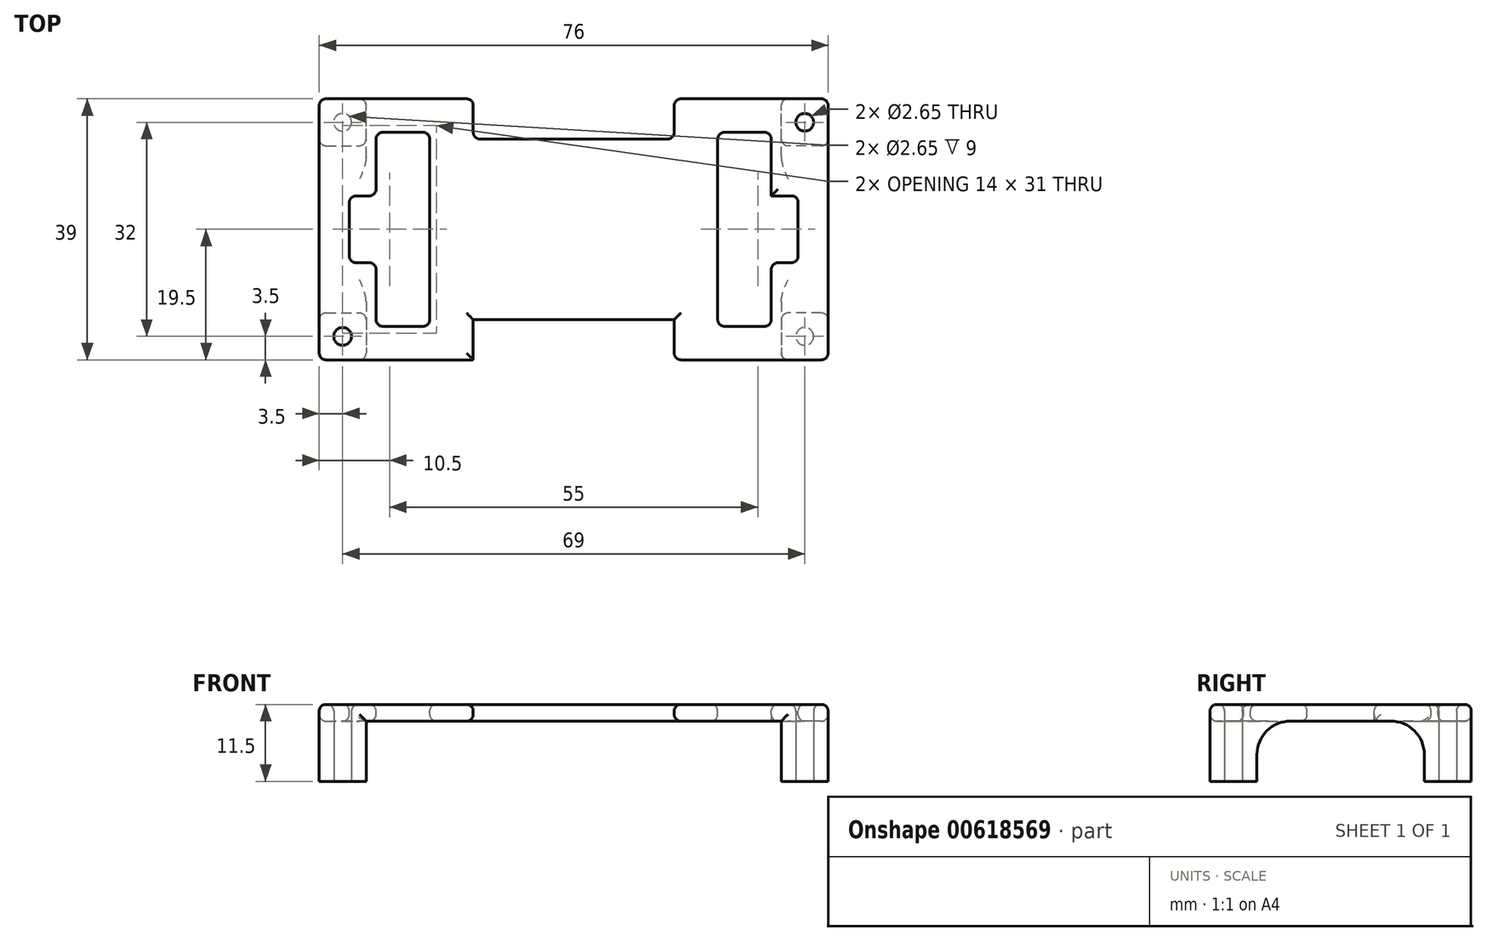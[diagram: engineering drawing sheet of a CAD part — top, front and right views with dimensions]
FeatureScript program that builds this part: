
annotation { "Feature Type Name" : "Feature", "Feature Type Description" : "" }
export const myFeature = defineFeature(function(context is Context, id is Id, definition is map)
    precondition{}
    {
        {
            var Q0;
            Q0=qCreatedBy(makeId("Top.planeOp"),FACE);
            var sketch = newSketch(context, id + "F0", { "sketchPlane" : qUnion([Q0])});
            skCircle(sketch, "E0", {"center": v(-34.5, 16) * mm, "radius": 1.5 * mm});
            skCircle(sketch, "E1", {"center": v(-34.5, 16) * mm, "radius": 1.32 * mm});
            skLineSegment(sketch, "E2", {"start": v(-38, 0) * mm, "end": v(-38, 19.5) * mm});
            skLineSegment(sketch, "E3", {"start": v(-38, 19.5) * mm, "end": v(0, 19.5) * mm});
            skLineSegment(sketch, "E4.MirrorCS", {"start": v(38, 19.5) * mm, "end": v(0, 19.5) * mm});
            skLineSegment(sketch, "E5.MirrorCS", {"start": v(-38, -19.5) * mm, "end": v(0, -19.5) * mm});
            skLineSegment(sketch, "E6.MirrorCS", {"start": v(38, -19.5) * mm, "end": v(0, -19.5) * mm});
            skLineSegment(sketch, "E7.MirrorCS", {"start": v(38, 0) * mm, "end": v(38, 19.5) * mm});
            skLineSegment(sketch, "E8.MirrorCS", {"start": v(-38, 0) * mm, "end": v(-38, -19.5) * mm});
            skLineSegment(sketch, "E9.MirrorCS", {"start": v(38, 0) * mm, "end": v(38, -19.5) * mm});
            skLineSegment(sketch, "E10", {"start": v(-38, 12.5) * mm, "end": v(-31, 12.5) * mm});
            skLineSegment(sketch, "E11", {"start": v(-31, 12.5) * mm, "end": v(-31, 19.5) * mm});
            skLineSegment(sketch, "E12.MirrorCS", {"start": v(31, 12.5) * mm, "end": v(31, 19.5) * mm});
            skLineSegment(sketch, "E13.MirrorCS", {"start": v(38, 12.5) * mm, "end": v(31, 12.5) * mm});
            skLineSegment(sketch, "E14.MirrorCS", {"start": v(38, -12.5) * mm, "end": v(31, -12.5) * mm});
            skLineSegment(sketch, "E15.MirrorCS", {"start": v(31, -12.5) * mm, "end": v(31, -19.5) * mm});
            skLineSegment(sketch, "E16.MirrorCS", {"start": v(-38, -12.5) * mm, "end": v(-31, -12.5) * mm});
            skLineSegment(sketch, "E17.MirrorCS", {"start": v(-31, -12.5) * mm, "end": v(-31, -19.5) * mm});
            skCircle(sketch, "E18.MirrorC", {"center": v(34.5, 16) * mm, "radius": 1.32 * mm});
            skCircle(sketch, "E19.MirrorC", {"center": v(-34.5, -16) * mm, "radius": 1.32 * mm});
            skCircle(sketch, "E20.MirrorC", {"center": v(34.5, -16) * mm, "radius": 1.32 * mm});
            skSolve(sketch);
        }
        {
            var Q0;
            Q0=makeQuery(id+"F0.imprint","IMPRINT",FACE,{"disambiguationData":[TD([[makeQuery(id+"F0.imprint","IMPRINT",EDGE,{"derivedFrom":sQuery(id+"F0.wireOp",EDGE,"E0")}),-1.0]])]});
            var Q1;
            Q1=makeQuery(id+"F0.imprint","IMPRINT",FACE,{"disambiguationData":[TD([[makeQuery(id+"F0.imprint","IMPRINT",EDGE,{"derivedFrom":sQuery(id+"F0.wireOp",EDGE,"9949ebb8-f0cd-4d5a-9bb0-dda6fca556a90.MirrorC")}),1.0]])]});
            var Q2;
            Q2=makeQuery(id+"F0.imprint","IMPRINT",FACE,{"disambiguationData":[TD([[makeQuery(id+"F0.imprint","IMPRINT",EDGE,{"derivedFrom":sQuery(id+"F0.wireOp",EDGE,"ff901f8d-6ad3-493e-a052-18a1848739b60.MirrorC")}),1.0]])]});
            var Q3;
            Q3=makeQuery(id+"F0.imprint","IMPRINT",FACE,{"disambiguationData":[TD([[makeQuery(id+"F0.imprint","IMPRINT",EDGE,{"derivedFrom":sQuery(id+"F0.wireOp",EDGE,"884a96e5-8a82-4bf0-9c84-4d8750a24e620.MirrorC")}),-1.0]])]});
            var Q4;
            {var subQ0=sQuery(id+"F0.wireOp",EDGE,"E16.MirrorCS");Q4=makeQuery(id+"F0.imprint","IMPRINT",FACE,{"disambiguationData":[TD([[makeQuery(id+"F0.imprint","IMPRINT",EDGE,{"derivedFrom":subQ0}),-1.0]])]});}
            var Q5;
            {var subQ1=sQuery(id+"F0.wireOp",EDGE,"E14.MirrorCS");Q5=makeQuery(id+"F0.imprint","IMPRINT",FACE,{"disambiguationData":[TD([[makeQuery(id+"F0.imprint","IMPRINT",EDGE,{"derivedFrom":subQ1}),1.0]])]});}
            var Q6;
            {var subQ0=sQuery(id+"F0.wireOp",EDGE,"E12.MirrorCS");Q6=makeQuery(id+"F0.imprint","IMPRINT",FACE,{"disambiguationData":[TD([[makeQuery(id+"F0.imprint","IMPRINT",EDGE,{"derivedFrom":subQ0}),-1.0]])]});}
            var Q7;
            Q7=makeQuery(id+"F0.imprint","IMPRINT",FACE,{"disambiguationData":[TD([[makeQuery(id+"F0.imprint","IMPRINT",EDGE,{"derivedFrom":sQuery(id+"F0.wireOp",EDGE,"E0")}),1.0]])]});
            extrude(context, id + "F1", {"entities" : qUnion([Q0, Q1, Q2, Q3, Q4, Q5, Q6, Q7]), "depth" : 9 * mm, "offsetDistance" : 25 * mm});
        }
        {
            var Q0;
            {var subQ13=sQuery(id+"F0.wireOp",EDGE,"E10");Q0=makeQuery(id+"F0.imprint","IMPRINT",FACE,{"disambiguationData":[TD([[makeQuery(id+"F0.imprint","IMPRINT",EDGE,{"derivedFrom":subQ13}),-1.0]])]});}
            var Q1;
            Q1=makeQuery(id+"F0.imprint","IMPRINT",FACE,{"disambiguationData":[TD([[makeQuery(id+"F0.imprint","IMPRINT",EDGE,{"derivedFrom":sQuery(id+"F0.wireOp",EDGE,"ff901f8d-6ad3-493e-a052-18a1848739b60.MirrorC")}),1.0]])]});
            var Q2;
            Q2=makeQuery(id+"F0.imprint","IMPRINT",FACE,{"disambiguationData":[TD([[makeQuery(id+"F0.imprint","IMPRINT",EDGE,{"derivedFrom":sQuery(id+"F0.wireOp",EDGE,"884a96e5-8a82-4bf0-9c84-4d8750a24e620.MirrorC")}),-1.0]])]});
            var Q3;
            Q3=makeQuery(id+"F0.imprint","IMPRINT",FACE,{"disambiguationData":[TD([[makeQuery(id+"F0.imprint","IMPRINT",EDGE,{"derivedFrom":sQuery(id+"F0.wireOp",EDGE,"ff901f8d-6ad3-493e-a052-18a1848739b60.MirrorC")}),-1.0]])]});
            var Q4;
            Q4=makeQuery(id+"F0.imprint","IMPRINT",FACE,{"disambiguationData":[TD([[makeQuery(id+"F0.imprint","IMPRINT",EDGE,{"derivedFrom":sQuery(id+"F0.wireOp",EDGE,"884a96e5-8a82-4bf0-9c84-4d8750a24e620.MirrorC")}),1.0]])]});
            var Q5;
            Q5=makeQuery(id+"F0.imprint","IMPRINT",FACE,{"disambiguationData":[TD([[makeQuery(id+"F0.imprint","IMPRINT",EDGE,{"derivedFrom":sQuery(id+"F0.wireOp",EDGE,"9949ebb8-f0cd-4d5a-9bb0-dda6fca556a90.MirrorC")}),1.0]])]});
            var Q6;
            Q6=makeQuery(id+"F0.imprint","IMPRINT",FACE,{"disambiguationData":[TD([[makeQuery(id+"F0.imprint","IMPRINT",EDGE,{"derivedFrom":sQuery(id+"F0.wireOp",EDGE,"9949ebb8-f0cd-4d5a-9bb0-dda6fca556a90.MirrorC")}),-1.0]])]});
            var Q7;
            {var subQ0=sQuery(id+"F0.wireOp",EDGE,"E12.MirrorCS");Q7=makeQuery(id+"F0.imprint","IMPRINT",FACE,{"disambiguationData":[TD([[makeQuery(id+"F0.imprint","IMPRINT",EDGE,{"derivedFrom":subQ0}),-1.0]])]});}
            var Q8;
            {var subQ1=sQuery(id+"F0.wireOp",EDGE,"E14.MirrorCS");Q8=makeQuery(id+"F0.imprint","IMPRINT",FACE,{"disambiguationData":[TD([[makeQuery(id+"F0.imprint","IMPRINT",EDGE,{"derivedFrom":subQ1}),1.0]])]});}
            var Q9;
            Q9=makeQuery(id+"F0.imprint","IMPRINT",FACE,{"disambiguationData":[TD([[makeQuery(id+"F0.imprint","IMPRINT",EDGE,{"derivedFrom":sQuery(id+"F0.wireOp",EDGE,"E0")}),-1.0]])]});
            var Q10;
            Q10=makeQuery(id+"F0.imprint","IMPRINT",FACE,{"disambiguationData":[TD([[makeQuery(id+"F0.imprint","IMPRINT",EDGE,{"derivedFrom":sQuery(id+"F0.wireOp",EDGE,"E0")}),1.0]])]});
            var Q11;
            Q11=makeQuery(id+"F0.imprint","IMPRINT",FACE,{"disambiguationData":[TD([[makeQuery(id+"F0.imprint","IMPRINT",EDGE,{"derivedFrom":sQuery(id+"F0.wireOp",EDGE,"E1")}),1.0]])]});
            var Q12;
            Q12=makeQuery(id+"F0.imprint","IMPRINT",FACE,{"disambiguationData":[TD([[makeQuery(id+"F0.imprint","IMPRINT",EDGE,{"derivedFrom":sQuery(id+"F0.wireOp",EDGE,"E18.MirrorC")}),-1.0]])]});
            var Q13;
            Q13=makeQuery(id+"F0.imprint","IMPRINT",FACE,{"disambiguationData":[TD([[makeQuery(id+"F0.imprint","IMPRINT",EDGE,{"derivedFrom":sQuery(id+"F0.wireOp",EDGE,"E20.MirrorC")}),1.0]])]});
            var Q14;
            {var subQ0=sQuery(id+"F0.wireOp",EDGE,"E16.MirrorCS");Q14=makeQuery(id+"F0.imprint","IMPRINT",FACE,{"disambiguationData":[TD([[makeQuery(id+"F0.imprint","IMPRINT",EDGE,{"derivedFrom":subQ0}),-1.0]])]});}
            var Q15;
            Q15=makeQuery(id+"F0.imprint","IMPRINT",FACE,{"disambiguationData":[TD([[makeQuery(id+"F0.imprint","IMPRINT",EDGE,{"derivedFrom":sQuery(id+"F0.wireOp",EDGE,"E19.MirrorC")}),-1.0]])]});
            extrude(context, id + "F2", {"entities" : qUnion([Q0, Q1, Q2, Q3, Q4, Q5, Q6, Q7, Q8, Q9, Q10, Q11, Q12, Q13, Q14, Q15]), "depth" : 11.5 * mm, "offsetDistance" : 25 * mm, "hasSecondDirection" : true, "secondDirectionOppositeDirection" : true, "secondDirectionDepth" : -9 * mm});
        }
        {
            var Q0;
            Q0=makeQuery(id+"F1.opExtrude","SWEPT_BODY",BODY,{"disambiguationData":[OSD([sQuery(id+"F0.wireOp",EDGE,"ff901f8d-6ad3-493e-a052-18a1848739b60.MirrorC"),sQuery(id+"F0.wireOp",EDGE,"E5.MirrorCS"),sQuery(id+"F0.wireOp",EDGE,"E8.MirrorCS"),sQuery(id+"F0.wireOp",EDGE,"E16.MirrorCS"),sQuery(id+"F0.wireOp",EDGE,"E17.MirrorCS")])]});
            var Q1;
            Q1=makeQuery(id+"F2.opExtrude","SWEPT_BODY",BODY,{"disambiguationData":[OSD([sQuery(id+"F0.wireOp",EDGE,"E2"),sQuery(id+"F0.wireOp",EDGE,"E3"),sQuery(id+"F0.wireOp",EDGE,"E4.MirrorCS"),sQuery(id+"F0.wireOp",EDGE,"E5.MirrorCS"),sQuery(id+"F0.wireOp",EDGE,"E6.MirrorCS"),sQuery(id+"F0.wireOp",EDGE,"E7.MirrorCS"),sQuery(id+"F0.wireOp",EDGE,"E8.MirrorCS"),sQuery(id+"F0.wireOp",EDGE,"E9.MirrorCS")])]});
            var Q2;
            Q2=makeQuery(id+"F1.opExtrude","SWEPT_BODY",BODY,{"disambiguationData":[OSD([sQuery(id+"F0.wireOp",EDGE,"E0"),sQuery(id+"F0.wireOp",EDGE,"E2"),sQuery(id+"F0.wireOp",EDGE,"E3"),sQuery(id+"F0.wireOp",EDGE,"E10"),sQuery(id+"F0.wireOp",EDGE,"E11")])]});
            var Q3;
            Q3=makeQuery(id+"F1.opExtrude","SWEPT_BODY",BODY,{"disambiguationData":[OSD([sQuery(id+"F0.wireOp",EDGE,"884a96e5-8a82-4bf0-9c84-4d8750a24e620.MirrorC"),sQuery(id+"F0.wireOp",EDGE,"E6.MirrorCS"),sQuery(id+"F0.wireOp",EDGE,"E9.MirrorCS"),sQuery(id+"F0.wireOp",EDGE,"E14.MirrorCS"),sQuery(id+"F0.wireOp",EDGE,"E15.MirrorCS")])]});
            var Q4;
            Q4=makeQuery(id+"F1.opExtrude","SWEPT_BODY",BODY,{"disambiguationData":[OSD([sQuery(id+"F0.wireOp",EDGE,"9949ebb8-f0cd-4d5a-9bb0-dda6fca556a90.MirrorC"),sQuery(id+"F0.wireOp",EDGE,"E4.MirrorCS"),sQuery(id+"F0.wireOp",EDGE,"E7.MirrorCS"),sQuery(id+"F0.wireOp",EDGE,"E12.MirrorCS"),sQuery(id+"F0.wireOp",EDGE,"E13.MirrorCS")])]});
            booleanBodies(context, id + "F3", {"operationType" : BooleanOperationType.UNION, "tools" : qUnion([Q0, Q1, Q2, Q3, Q4])});
        }
        {
            var Q0;
            Q0=makeQuery(id+"F1.opExtrude","CAP_EDGE",EDGE,{"disambiguationData":[OSD([sQuery(id+"F0.wireOp",EDGE,"E16.MirrorCS")])],"isStart":false});
            var Q1;
            Q1=makeQuery(id+"F1.opExtrude","CAP_EDGE",EDGE,{"disambiguationData":[OSD([sQuery(id+"F0.wireOp",EDGE,"E10")])],"isStart":false});
            var Q2;
            Q2=makeQuery(id+"F1.opExtrude","CAP_EDGE",EDGE,{"disambiguationData":[OSD([sQuery(id+"F0.wireOp",EDGE,"E14.MirrorCS")])],"isStart":false});
            var Q3;
            Q3=makeQuery(id+"F1.opExtrude","CAP_EDGE",EDGE,{"disambiguationData":[OSD([sQuery(id+"F0.wireOp",EDGE,"E13.MirrorCS")])],"isStart":false});
            fillet(context, id + "F4", {"entities" : qUnion([Q0, Q1, Q2, Q3]), "radius" : 5 * mm, "tangentPropagation" : true, "allowEdgeOverflow" : false});
        }
        {
            var Q0;
            Q0=makeQuery(id+"F2.opExtrude","CAP_FACE",FACE,{"disambiguationData":[OSD([sQuery(id+"F0.wireOp",EDGE,"E2"),sQuery(id+"F0.wireOp",EDGE,"E3"),sQuery(id+"F0.wireOp",EDGE,"E4.MirrorCS"),sQuery(id+"F0.wireOp",EDGE,"E5.MirrorCS"),sQuery(id+"F0.wireOp",EDGE,"E6.MirrorCS"),sQuery(id+"F0.wireOp",EDGE,"E7.MirrorCS"),sQuery(id+"F0.wireOp",EDGE,"E8.MirrorCS"),sQuery(id+"F0.wireOp",EDGE,"E9.MirrorCS")])],"isStart":false});
            var sketch = newSketch(context, id + "F5", { "sketchPlane" : qUnion([Q0])});
            skLineSegment(sketch, "E21", {"start": v(0, 19.5) * mm, "end": v(0, -19.5) * mm, "construction": true});
            skLineSegment(sketch, "E22", {"start": v(-38, 0) * mm, "end": v(38, 0) * mm, "construction": true});
            skLineSegment(sketch, "E23.bottom", {"start": v(-25, 25) * mm, "end": v(25, 25) * mm, "construction": true});
            skLineSegment(sketch, "E23.top", {"start": v(-25, -25) * mm, "end": v(25, -25) * mm, "construction": true});
            skLineSegment(sketch, "E23.left", {"start": v(-25, 25) * mm, "end": v(-25, -25) * mm, "construction": true});
            skLineSegment(sketch, "E23.right", {"start": v(25, 25) * mm, "end": v(25, -25) * mm, "construction": true});
            skLineSegment(sketch, "E24.bottom", {"start": v(-29.5, -14.5) * mm, "end": v(-21.5, -14.5) * mm});
            skLineSegment(sketch, "E24.top", {"start": v(-29.5, 14.5) * mm, "end": v(-21.5, 14.5) * mm});
            skLineSegment(sketch, "E24.left", {"start": v(-29.5, -14.5) * mm, "end": v(-29.5, 14.5) * mm});
            skLineSegment(sketch, "E24.right", {"start": v(-21.5, -14.5) * mm, "end": v(-21.5, 14.5) * mm});
            skLineSegment(sketch, "E25.0", {"start": v(-31, -12.5) * mm, "end": v(-31, -7.5) * mm});
            skLineSegment(sketch, "E26.MirrorCS", {"start": v(21.5, -14.5) * mm, "end": v(21.5, 14.5) * mm});
            skLineSegment(sketch, "E27.MirrorCS", {"start": v(29.5, 14.5) * mm, "end": v(21.5, 14.5) * mm});
            skLineSegment(sketch, "E28.MirrorCS", {"start": v(29.5, -14.5) * mm, "end": v(29.5, 14.5) * mm});
            skLineSegment(sketch, "E29.MirrorCS", {"start": v(29.5, -14.5) * mm, "end": v(21.5, -14.5) * mm});
            skLineSegment(sketch, "E30.bottom", {"start": v(-29.5, -5) * mm, "end": v(-33.5, -5) * mm});
            skLineSegment(sketch, "E30.top", {"start": v(-29.5, 5) * mm, "end": v(-33.5, 5) * mm});
            skLineSegment(sketch, "E30.left", {"start": v(-29.5, -5) * mm, "end": v(-29.5, 5) * mm});
            skLineSegment(sketch, "E30.right", {"start": v(-33.5, -5) * mm, "end": v(-33.5, 5) * mm});
            skLineSegment(sketch, "E31", {"start": v(-33.5, 0) * mm, "end": v(-29.5, 0) * mm, "construction": true});
            skLineSegment(sketch, "E32.MirrorCS", {"start": v(29.5, 5) * mm, "end": v(33.5, 5) * mm});
            skLineSegment(sketch, "E33.MirrorCS", {"start": v(33.5, -5) * mm, "end": v(33.5, 5) * mm});
            skLineSegment(sketch, "E34.MirrorCS", {"start": v(29.5, -5) * mm, "end": v(33.5, -5) * mm});
            skLineSegment(sketch, "E35.bottom", {"start": v(-15, -19.5) * mm, "end": v(15, -19.5) * mm});
            skLineSegment(sketch, "E35.top", {"start": v(-15, -13.5) * mm, "end": v(15, -13.5) * mm});
            skLineSegment(sketch, "E35.left", {"start": v(-15, -19.5) * mm, "end": v(-15, -13.5) * mm});
            skLineSegment(sketch, "E35.right", {"start": v(15, -19.5) * mm, "end": v(15, -13.5) * mm});
            skLineSegment(sketch, "E36", {"start": v(0, -13.5) * mm, "end": v(0, -19.5) * mm, "construction": true});
            skLineSegment(sketch, "E37.MirrorCS", {"start": v(-15, 13.5) * mm, "end": v(15, 13.5) * mm});
            skLineSegment(sketch, "E38.MirrorCS", {"start": v(-15, 19.5) * mm, "end": v(-15, 13.5) * mm});
            skLineSegment(sketch, "E39.MirrorCS", {"start": v(15, 19.5) * mm, "end": v(15, 13.5) * mm});
            skSolve(sketch);
        }
        {
            var Q0;
            Q0 = qSketchRegion(id + "F5", true);
            var Q1;
            Q1=makeQuery(id+"F5.imprint","IMPRINT",FACE,{"disambiguationData":[TD([[makeQuery(id+"F5.imprint","IMPRINT",EDGE,{"derivedFrom":sQuery(id+"F5.wireOp",EDGE,"E37.MirrorCS")}),1.0]])]});
            extrude(context, id + "F6", {"entities" : qUnion([Q0, Q1]), "operationType" : NewBodyOperationType.REMOVE, "oppositeDirection" : true, "depth" : 10 * mm, "offsetDistance" : 25 * mm});
        }
        {
            var Q0;
            Q0=makeQuery(id+"F2.opExtrude","CAP_FACE",FACE,{"disambiguationData":[OSD([sQuery(id+"F0.wireOp",EDGE,"E2"),sQuery(id+"F0.wireOp",EDGE,"E3"),sQuery(id+"F0.wireOp",EDGE,"E4.MirrorCS"),sQuery(id+"F0.wireOp",EDGE,"E5.MirrorCS"),sQuery(id+"F0.wireOp",EDGE,"E6.MirrorCS"),sQuery(id+"F0.wireOp",EDGE,"E7.MirrorCS"),sQuery(id+"F0.wireOp",EDGE,"E8.MirrorCS"),sQuery(id+"F0.wireOp",EDGE,"E9.MirrorCS")])],"isStart":false});
            var Q1;
            {var subQ0=sQuery(id+"F0.wireOp",EDGE,"E9.MirrorCS");var subQ1=sQuery(id+"F0.wireOp",EDGE,"E8.MirrorCS");var subQ2=sQuery(id+"F0.wireOp",EDGE,"E7.MirrorCS");var subQ3=sQuery(id+"F0.wireOp",EDGE,"E6.MirrorCS");var subQ4=sQuery(id+"F0.wireOp",EDGE,"E2");var subQ5=sQuery(id+"F0.wireOp",EDGE,"E4.MirrorCS");var subQ6=sQuery(id+"F0.wireOp",EDGE,"E3");var subQ7=sQuery(id+"F0.wireOp",EDGE,"E5.MirrorCS");Q1=makeQuery(id+"F6.boolean.opBoolean","INTERSECT",EDGE,{"derivedFrom":[makeQuery(id+"F3.opBoolean","SPLIT",FACE,{"disambiguationData":[TD([makeQuery(id+"F1.opExtrude","SWEPT_FACE",FACE,{"disambiguationData":[OSD([subQ4])]})])],"derivedFrom":makeQuery(id+"F2.opExtrude","CAP_FACE",FACE,{"disambiguationData":[OSD([subQ4,subQ6,subQ5,subQ7,subQ3,subQ2,subQ1,subQ0])],"isStart":true})}),makeQuery(id+"F6.opExtrude","SWEPT_FACE",FACE,{"disambiguationData":[OSD([sQuery(id+"F5.wireOp",EDGE,"E35.top")])]})]});}
            var Q2;
            {var subQ0=sQuery(id+"F0.wireOp",EDGE,"E9.MirrorCS");var subQ1=sQuery(id+"F0.wireOp",EDGE,"E8.MirrorCS");var subQ2=sQuery(id+"F0.wireOp",EDGE,"E7.MirrorCS");var subQ3=sQuery(id+"F0.wireOp",EDGE,"E6.MirrorCS");var subQ4=sQuery(id+"F0.wireOp",EDGE,"E2");var subQ5=sQuery(id+"F0.wireOp",EDGE,"E4.MirrorCS");var subQ6=sQuery(id+"F0.wireOp",EDGE,"E3");var subQ7=sQuery(id+"F0.wireOp",EDGE,"E5.MirrorCS");Q2=makeQuery(id+"F6.boolean.opBoolean","INTERSECT",EDGE,{"derivedFrom":[makeQuery(id+"F3.opBoolean","SPLIT",FACE,{"disambiguationData":[TD([makeQuery(id+"F1.opExtrude","SWEPT_FACE",FACE,{"disambiguationData":[OSD([subQ4])]})])],"derivedFrom":makeQuery(id+"F2.opExtrude","CAP_FACE",FACE,{"disambiguationData":[OSD([subQ4,subQ6,subQ5,subQ7,subQ3,subQ2,subQ1,subQ0])],"isStart":true})}),makeQuery(id+"F6.opExtrude","SWEPT_FACE",FACE,{"disambiguationData":[OSD([sQuery(id+"F5.wireOp",EDGE,"E37.MirrorCS")])]})]});}
            var Q3;
            {var subQ0=sQuery(id+"F0.wireOp",EDGE,"E9.MirrorCS");var subQ1=sQuery(id+"F0.wireOp",EDGE,"E8.MirrorCS");var subQ2=sQuery(id+"F0.wireOp",EDGE,"E7.MirrorCS");var subQ3=sQuery(id+"F0.wireOp",EDGE,"E6.MirrorCS");var subQ4=sQuery(id+"F0.wireOp",EDGE,"E2");var subQ5=sQuery(id+"F0.wireOp",EDGE,"E4.MirrorCS");var subQ6=sQuery(id+"F0.wireOp",EDGE,"E3");var subQ7=sQuery(id+"F0.wireOp",EDGE,"E5.MirrorCS");Q3=makeQuery(id+"F6.boolean.opBoolean","INTERSECT",EDGE,{"derivedFrom":[makeQuery(id+"F3.opBoolean","SPLIT",FACE,{"disambiguationData":[TD([makeQuery(id+"F1.opExtrude","SWEPT_FACE",FACE,{"disambiguationData":[OSD([subQ4])]})])],"derivedFrom":makeQuery(id+"F2.opExtrude","CAP_FACE",FACE,{"disambiguationData":[OSD([subQ4,subQ6,subQ5,subQ7,subQ3,subQ2,subQ1,subQ0])],"isStart":true})}),makeQuery(id+"F6.opExtrude","SWEPT_FACE",FACE,{"disambiguationData":[OSD([sQuery(id+"F5.wireOp",EDGE,"E38.MirrorCS")])]})]});}
            var Q4;
            Q4=makeQuery(id+"F6.boolean.opBoolean","COPY",EDGE,{"derivedFrom":makeQuery(id+"F6.opExtrude","SWEPT_EDGE",EDGE,{"disambiguationData":[OSD([sQuery(id+"F5.wireOp",EDGE,"E37.MirrorCS"),sQuery(id+"F5.wireOp",EDGE,"E38.MirrorCS")])]})});
            var Q5;
            Q5=makeQuery(id+"F6.boolean.opBoolean","COPY",EDGE,{"derivedFrom":makeQuery(id+"F6.opExtrude","SWEPT_EDGE",EDGE,{"disambiguationData":[OSD([sQuery(id+"F0.wireOp",EDGE,"E3"),sQuery(id+"F0.wireOp",EDGE,"E4.MirrorCS"),sQuery(id+"F5.wireOp",EDGE,"E38.MirrorCS")])]})});
            var Q6;
            Q6=makeQuery(id+"F6.boolean.opBoolean","COPY",EDGE,{"derivedFrom":makeQuery(id+"F6.opExtrude","SWEPT_EDGE",EDGE,{"disambiguationData":[OSD([sQuery(id+"F0.wireOp",EDGE,"E3"),sQuery(id+"F0.wireOp",EDGE,"E4.MirrorCS"),sQuery(id+"F5.wireOp",EDGE,"E39.MirrorCS")])]})});
            var Q7;
            {var subQ0=sQuery(id+"F0.wireOp",EDGE,"E4.MirrorCS");var subQ1=sQuery(id+"F0.wireOp",EDGE,"E3");Q7=makeQuery(id+"F6.boolean.opBoolean","SPLIT",EDGE,{"disambiguationData":[TD([makeQuery(id+"F1.opExtrude","SWEPT_FACE",FACE,{"disambiguationData":[OSD([sQuery(id+"F0.wireOp",EDGE,"E12.MirrorCS")])]})])],"derivedFrom":makeQuery(id+"F2.opExtrude","CAP_EDGE",EDGE,{"disambiguationData":[OSD([subQ1,subQ0])],"isStart":true})});}
            var Q8;
            {var subQ0=sQuery(id+"F0.wireOp",EDGE,"E9.MirrorCS");var subQ1=sQuery(id+"F0.wireOp",EDGE,"E8.MirrorCS");var subQ2=sQuery(id+"F0.wireOp",EDGE,"E7.MirrorCS");var subQ3=sQuery(id+"F0.wireOp",EDGE,"E6.MirrorCS");var subQ4=sQuery(id+"F0.wireOp",EDGE,"E2");var subQ5=sQuery(id+"F0.wireOp",EDGE,"E4.MirrorCS");var subQ6=sQuery(id+"F0.wireOp",EDGE,"E3");var subQ7=sQuery(id+"F0.wireOp",EDGE,"E5.MirrorCS");Q8=makeQuery(id+"F6.boolean.opBoolean","INTERSECT",EDGE,{"derivedFrom":[makeQuery(id+"F3.opBoolean","SPLIT",FACE,{"disambiguationData":[TD([makeQuery(id+"F1.opExtrude","SWEPT_FACE",FACE,{"disambiguationData":[OSD([subQ4])]})])],"derivedFrom":makeQuery(id+"F2.opExtrude","CAP_FACE",FACE,{"disambiguationData":[OSD([subQ4,subQ6,subQ5,subQ7,subQ3,subQ2,subQ1,subQ0])],"isStart":true})}),makeQuery(id+"F6.opExtrude","SWEPT_FACE",FACE,{"disambiguationData":[OSD([sQuery(id+"F5.wireOp",EDGE,"E35.right")])]})]});}
            var Q9;
            Q9=makeQuery(id+"F6.boolean.opBoolean","COPY",EDGE,{"derivedFrom":makeQuery(id+"F6.opExtrude","SWEPT_EDGE",EDGE,{"disambiguationData":[OSD([sQuery(id+"F0.wireOp",EDGE,"E5.MirrorCS"),sQuery(id+"F0.wireOp",EDGE,"E6.MirrorCS"),sQuery(id+"F5.wireOp",EDGE,"E35.bottom"),sQuery(id+"F5.wireOp",EDGE,"E35.right")])]})});
            var Q10;
            {var subQ0=sQuery(id+"F0.wireOp",EDGE,"E9.MirrorCS");var subQ1=sQuery(id+"F0.wireOp",EDGE,"E8.MirrorCS");var subQ2=sQuery(id+"F0.wireOp",EDGE,"E7.MirrorCS");var subQ3=sQuery(id+"F0.wireOp",EDGE,"E6.MirrorCS");var subQ4=sQuery(id+"F0.wireOp",EDGE,"E2");var subQ5=sQuery(id+"F0.wireOp",EDGE,"E4.MirrorCS");var subQ6=sQuery(id+"F0.wireOp",EDGE,"E3");var subQ7=sQuery(id+"F0.wireOp",EDGE,"E5.MirrorCS");Q10=makeQuery(id+"F6.boolean.opBoolean","INTERSECT",EDGE,{"derivedFrom":[makeQuery(id+"F3.opBoolean","SPLIT",FACE,{"disambiguationData":[TD([makeQuery(id+"F1.opExtrude","SWEPT_FACE",FACE,{"disambiguationData":[OSD([subQ4])]})])],"derivedFrom":makeQuery(id+"F2.opExtrude","CAP_FACE",FACE,{"disambiguationData":[OSD([subQ4,subQ6,subQ5,subQ7,subQ3,subQ2,subQ1,subQ0])],"isStart":true})}),makeQuery(id+"F6.opExtrude","SWEPT_FACE",FACE,{"disambiguationData":[OSD([sQuery(id+"F5.wireOp",EDGE,"E35.left")])]})]});}
            var Q11;
            Q11=makeQuery(id+"F6.boolean.opBoolean","COPY",EDGE,{"derivedFrom":makeQuery(id+"F6.opExtrude","SWEPT_EDGE",EDGE,{"disambiguationData":[OSD([sQuery(id+"F0.wireOp",EDGE,"E5.MirrorCS"),sQuery(id+"F0.wireOp",EDGE,"E6.MirrorCS"),sQuery(id+"F5.wireOp",EDGE,"E35.bottom"),sQuery(id+"F5.wireOp",EDGE,"E35.left")])]})});
            var Q12;
            {var subQ0=sQuery(id+"F0.wireOp",EDGE,"E3");var subQ1=sQuery(id+"F0.wireOp",EDGE,"E2");Q12=makeQuery(id+"F3.opBoolean","MERGE",EDGE,{"derivedFrom":[makeQuery(id+"F1.opExtrude","SWEPT_EDGE",EDGE,{"disambiguationData":[OSD([subQ1,subQ0])]}),makeQuery(id+"F2.opExtrude","SWEPT_EDGE",EDGE,{"disambiguationData":[OSD([subQ1,subQ0])]})]});}
            var Q13;
            {var subQ0=sQuery(id+"F0.wireOp",EDGE,"E8.MirrorCS");var subQ1=sQuery(id+"F0.wireOp",EDGE,"E5.MirrorCS");Q13=makeQuery(id+"F3.opBoolean","MERGE",EDGE,{"derivedFrom":[makeQuery(id+"F1.opExtrude","SWEPT_EDGE",EDGE,{"disambiguationData":[OSD([subQ1,subQ0])]}),makeQuery(id+"F2.opExtrude","SWEPT_EDGE",EDGE,{"disambiguationData":[OSD([subQ1,subQ0])]})]});}
            var Q14;
            Q14=makeQuery(id+"F1.opExtrude","SWEPT_EDGE",EDGE,{"disambiguationData":[OSD([sQuery(id+"F0.wireOp",EDGE,"E5.MirrorCS"),sQuery(id+"F0.wireOp",EDGE,"E17.MirrorCS")])]});
            var Q15;
            {var subQ0=sQuery(id+"F0.wireOp",EDGE,"E6.MirrorCS");var subQ1=sQuery(id+"F0.wireOp",EDGE,"E5.MirrorCS");Q15=makeQuery(id+"F6.boolean.opBoolean","SPLIT",EDGE,{"disambiguationData":[TD([makeQuery(id+"F1.opExtrude","SWEPT_FACE",FACE,{"disambiguationData":[OSD([sQuery(id+"F0.wireOp",EDGE,"E17.MirrorCS")])]})])],"derivedFrom":makeQuery(id+"F2.opExtrude","CAP_EDGE",EDGE,{"disambiguationData":[OSD([subQ1,subQ0])],"isStart":true})});}
            var Q16;
            Q16=makeQuery(id+"F1.opExtrude","SWEPT_EDGE",EDGE,{"disambiguationData":[OSD([sQuery(id+"F0.wireOp",EDGE,"E3"),sQuery(id+"F0.wireOp",EDGE,"E11")])]});
            var Q17;
            {var subQ0=sQuery(id+"F0.wireOp",EDGE,"E4.MirrorCS");var subQ1=sQuery(id+"F0.wireOp",EDGE,"E3");Q17=makeQuery(id+"F6.boolean.opBoolean","SPLIT",EDGE,{"disambiguationData":[TD([makeQuery(id+"F1.opExtrude","SWEPT_FACE",FACE,{"disambiguationData":[OSD([sQuery(id+"F0.wireOp",EDGE,"E11")])]})])],"derivedFrom":makeQuery(id+"F2.opExtrude","CAP_EDGE",EDGE,{"disambiguationData":[OSD([subQ1,subQ0])],"isStart":true})});}
            var Q18;
            Q18=makeQuery(id+"F1.opExtrude","SWEPT_EDGE",EDGE,{"disambiguationData":[OSD([sQuery(id+"F0.wireOp",EDGE,"E4.MirrorCS"),sQuery(id+"F0.wireOp",EDGE,"E12.MirrorCS")])]});
            var Q19;
            {var subQ0=sQuery(id+"F0.wireOp",EDGE,"E7.MirrorCS");var subQ1=sQuery(id+"F0.wireOp",EDGE,"E4.MirrorCS");Q19=makeQuery(id+"F3.opBoolean","MERGE",EDGE,{"derivedFrom":[makeQuery(id+"F1.opExtrude","SWEPT_EDGE",EDGE,{"disambiguationData":[OSD([subQ1,subQ0])]}),makeQuery(id+"F2.opExtrude","SWEPT_EDGE",EDGE,{"disambiguationData":[OSD([subQ1,subQ0])]})]});}
            var Q20;
            {var subQ0=sQuery(id+"F0.wireOp",EDGE,"E9.MirrorCS");var subQ1=sQuery(id+"F0.wireOp",EDGE,"E6.MirrorCS");Q20=makeQuery(id+"F3.opBoolean","MERGE",EDGE,{"derivedFrom":[makeQuery(id+"F1.opExtrude","SWEPT_EDGE",EDGE,{"disambiguationData":[OSD([subQ1,subQ0])]}),makeQuery(id+"F2.opExtrude","SWEPT_EDGE",EDGE,{"disambiguationData":[OSD([subQ1,subQ0])]})]});}
            var Q21;
            Q21=makeQuery(id+"F1.opExtrude","SWEPT_EDGE",EDGE,{"disambiguationData":[OSD([sQuery(id+"F0.wireOp",EDGE,"E6.MirrorCS"),sQuery(id+"F0.wireOp",EDGE,"E15.MirrorCS")])]});
            var Q22;
            {var subQ0=sQuery(id+"F0.wireOp",EDGE,"E6.MirrorCS");var subQ1=sQuery(id+"F0.wireOp",EDGE,"E5.MirrorCS");Q22=makeQuery(id+"F6.boolean.opBoolean","SPLIT",EDGE,{"disambiguationData":[TD([makeQuery(id+"F1.opExtrude","SWEPT_FACE",FACE,{"disambiguationData":[OSD([sQuery(id+"F0.wireOp",EDGE,"E15.MirrorCS")])]})])],"derivedFrom":makeQuery(id+"F2.opExtrude","CAP_EDGE",EDGE,{"disambiguationData":[OSD([subQ1,subQ0])],"isStart":true})});}
            var Q23;
            Q23=makeQuery(id+"F6.boolean.opBoolean","COPY",FACE,{"derivedFrom":makeQuery(id+"F6.opExtrude","SWEPT_FACE",FACE,{"disambiguationData":[OSD([sQuery(id+"F5.wireOp",EDGE,"E39.MirrorCS")])]})});
            var Q24;
            {var subQ0=sQuery(id+"F5.wireOp",EDGE,"E24.left");var subQ1=sQuery(id+"F0.wireOp",EDGE,"E9.MirrorCS");var subQ2=sQuery(id+"F0.wireOp",EDGE,"E8.MirrorCS");var subQ3=sQuery(id+"F0.wireOp",EDGE,"E7.MirrorCS");var subQ4=sQuery(id+"F0.wireOp",EDGE,"E6.MirrorCS");var subQ5=sQuery(id+"F0.wireOp",EDGE,"E2");var subQ6=sQuery(id+"F0.wireOp",EDGE,"E4.MirrorCS");var subQ7=sQuery(id+"F0.wireOp",EDGE,"E3");var subQ8=sQuery(id+"F0.wireOp",EDGE,"E5.MirrorCS");Q24=makeQuery(id+"F6.boolean.opBoolean","INTERSECT",EDGE,{"derivedFrom":[makeQuery(id+"F3.opBoolean","SPLIT",FACE,{"disambiguationData":[TD([makeQuery(id+"F1.opExtrude","SWEPT_FACE",FACE,{"disambiguationData":[OSD([subQ5])]})])],"derivedFrom":makeQuery(id+"F2.opExtrude","CAP_FACE",FACE,{"disambiguationData":[OSD([subQ5,subQ7,subQ6,subQ8,subQ4,subQ3,subQ2,subQ1])],"isStart":true})}),makeQuery(id+"F6.opExtrude","SWEPT_FACE",FACE,{"disambiguationData":[OSD([subQ0]),TDD([makeQuery(id+"F5.imprint","IMPRINT",EDGE,{"disambiguationData":[TD([[makeQuery(id+"F5.imprint","INTERSECT",VERTEX,{"derivedFrom":[sQuery(id+"F5.wireOp",EDGE,"E24.bottom"),subQ0]}),-1.0]])],"derivedFrom":subQ0})])]})]});}
            var Q25;
            {var subQ0=sQuery(id+"F0.wireOp",EDGE,"E9.MirrorCS");var subQ1=sQuery(id+"F0.wireOp",EDGE,"E8.MirrorCS");var subQ2=sQuery(id+"F0.wireOp",EDGE,"E7.MirrorCS");var subQ3=sQuery(id+"F0.wireOp",EDGE,"E6.MirrorCS");var subQ4=sQuery(id+"F0.wireOp",EDGE,"E2");var subQ5=sQuery(id+"F0.wireOp",EDGE,"E4.MirrorCS");var subQ6=sQuery(id+"F0.wireOp",EDGE,"E3");var subQ7=sQuery(id+"F0.wireOp",EDGE,"E5.MirrorCS");Q25=makeQuery(id+"F6.boolean.opBoolean","INTERSECT",EDGE,{"derivedFrom":[makeQuery(id+"F3.opBoolean","SPLIT",FACE,{"disambiguationData":[TD([makeQuery(id+"F1.opExtrude","SWEPT_FACE",FACE,{"disambiguationData":[OSD([subQ4])]})])],"derivedFrom":makeQuery(id+"F2.opExtrude","CAP_FACE",FACE,{"disambiguationData":[OSD([subQ4,subQ6,subQ5,subQ7,subQ3,subQ2,subQ1,subQ0])],"isStart":true})}),makeQuery(id+"F6.opExtrude","SWEPT_FACE",FACE,{"disambiguationData":[OSD([sQuery(id+"F5.wireOp",EDGE,"E30.bottom")])]})]});}
            var Q26;
            Q26=makeQuery(id+"F6.boolean.opBoolean","COPY",FACE,{"derivedFrom":makeQuery(id+"F6.opExtrude","SWEPT_FACE",FACE,{"disambiguationData":[OSD([sQuery(id+"F5.wireOp",EDGE,"E30.right")])]})});
            var Q27;
            {var subQ0=sQuery(id+"F0.wireOp",EDGE,"E9.MirrorCS");var subQ1=sQuery(id+"F0.wireOp",EDGE,"E8.MirrorCS");var subQ2=sQuery(id+"F0.wireOp",EDGE,"E7.MirrorCS");var subQ3=sQuery(id+"F0.wireOp",EDGE,"E6.MirrorCS");var subQ4=sQuery(id+"F0.wireOp",EDGE,"E2");var subQ5=sQuery(id+"F0.wireOp",EDGE,"E4.MirrorCS");var subQ6=sQuery(id+"F0.wireOp",EDGE,"E3");var subQ7=sQuery(id+"F0.wireOp",EDGE,"E5.MirrorCS");Q27=makeQuery(id+"F6.boolean.opBoolean","INTERSECT",EDGE,{"derivedFrom":[makeQuery(id+"F3.opBoolean","SPLIT",FACE,{"disambiguationData":[TD([makeQuery(id+"F1.opExtrude","SWEPT_FACE",FACE,{"disambiguationData":[OSD([subQ4])]})])],"derivedFrom":makeQuery(id+"F2.opExtrude","CAP_FACE",FACE,{"disambiguationData":[OSD([subQ4,subQ6,subQ5,subQ7,subQ3,subQ2,subQ1,subQ0])],"isStart":true})}),makeQuery(id+"F6.opExtrude","SWEPT_FACE",FACE,{"disambiguationData":[OSD([sQuery(id+"F5.wireOp",EDGE,"E24.bottom")])]})]});}
            var Q28;
            {var subQ0=sQuery(id+"F0.wireOp",EDGE,"E9.MirrorCS");var subQ1=sQuery(id+"F0.wireOp",EDGE,"E8.MirrorCS");var subQ2=sQuery(id+"F0.wireOp",EDGE,"E7.MirrorCS");var subQ3=sQuery(id+"F0.wireOp",EDGE,"E6.MirrorCS");var subQ4=sQuery(id+"F0.wireOp",EDGE,"E2");var subQ5=sQuery(id+"F0.wireOp",EDGE,"E4.MirrorCS");var subQ6=sQuery(id+"F0.wireOp",EDGE,"E3");var subQ7=sQuery(id+"F0.wireOp",EDGE,"E5.MirrorCS");Q28=makeQuery(id+"F6.boolean.opBoolean","INTERSECT",EDGE,{"derivedFrom":[makeQuery(id+"F3.opBoolean","SPLIT",FACE,{"disambiguationData":[TD([makeQuery(id+"F1.opExtrude","SWEPT_FACE",FACE,{"disambiguationData":[OSD([subQ4])]})])],"derivedFrom":makeQuery(id+"F2.opExtrude","CAP_FACE",FACE,{"disambiguationData":[OSD([subQ4,subQ6,subQ5,subQ7,subQ3,subQ2,subQ1,subQ0])],"isStart":true})}),makeQuery(id+"F6.opExtrude","SWEPT_FACE",FACE,{"disambiguationData":[OSD([sQuery(id+"F5.wireOp",EDGE,"E24.right")])]})]});}
            var Q29;
            {var subQ0=sQuery(id+"F0.wireOp",EDGE,"E9.MirrorCS");var subQ1=sQuery(id+"F0.wireOp",EDGE,"E8.MirrorCS");var subQ2=sQuery(id+"F0.wireOp",EDGE,"E7.MirrorCS");var subQ3=sQuery(id+"F0.wireOp",EDGE,"E6.MirrorCS");var subQ4=sQuery(id+"F0.wireOp",EDGE,"E2");var subQ5=sQuery(id+"F0.wireOp",EDGE,"E4.MirrorCS");var subQ6=sQuery(id+"F0.wireOp",EDGE,"E3");var subQ7=sQuery(id+"F0.wireOp",EDGE,"E5.MirrorCS");Q29=makeQuery(id+"F6.boolean.opBoolean","INTERSECT",EDGE,{"derivedFrom":[makeQuery(id+"F3.opBoolean","SPLIT",FACE,{"disambiguationData":[TD([makeQuery(id+"F1.opExtrude","SWEPT_FACE",FACE,{"disambiguationData":[OSD([subQ4])]})])],"derivedFrom":makeQuery(id+"F2.opExtrude","CAP_FACE",FACE,{"disambiguationData":[OSD([subQ4,subQ6,subQ5,subQ7,subQ3,subQ2,subQ1,subQ0])],"isStart":true})}),makeQuery(id+"F6.opExtrude","SWEPT_FACE",FACE,{"disambiguationData":[OSD([sQuery(id+"F5.wireOp",EDGE,"E24.top")])]})]});}
            var Q30;
            {var subQ0=sQuery(id+"F5.wireOp",EDGE,"E24.left");var subQ1=sQuery(id+"F0.wireOp",EDGE,"E9.MirrorCS");var subQ2=sQuery(id+"F0.wireOp",EDGE,"E8.MirrorCS");var subQ3=sQuery(id+"F0.wireOp",EDGE,"E7.MirrorCS");var subQ4=sQuery(id+"F0.wireOp",EDGE,"E6.MirrorCS");var subQ5=sQuery(id+"F0.wireOp",EDGE,"E2");var subQ6=sQuery(id+"F0.wireOp",EDGE,"E4.MirrorCS");var subQ7=sQuery(id+"F0.wireOp",EDGE,"E3");var subQ8=sQuery(id+"F0.wireOp",EDGE,"E5.MirrorCS");Q30=makeQuery(id+"F6.boolean.opBoolean","INTERSECT",EDGE,{"derivedFrom":[makeQuery(id+"F3.opBoolean","SPLIT",FACE,{"disambiguationData":[TD([makeQuery(id+"F1.opExtrude","SWEPT_FACE",FACE,{"disambiguationData":[OSD([subQ5])]})])],"derivedFrom":makeQuery(id+"F2.opExtrude","CAP_FACE",FACE,{"disambiguationData":[OSD([subQ5,subQ7,subQ6,subQ8,subQ4,subQ3,subQ2,subQ1])],"isStart":true})}),makeQuery(id+"F6.opExtrude","SWEPT_FACE",FACE,{"disambiguationData":[OSD([subQ0]),TDD([makeQuery(id+"F5.imprint","IMPRINT",EDGE,{"disambiguationData":[TD([[makeQuery(id+"F5.imprint","INTERSECT",VERTEX,{"derivedFrom":[sQuery(id+"F5.wireOp",EDGE,"E24.top"),subQ0]}),1.0]])],"derivedFrom":subQ0})])]})]});}
            var Q31;
            Q31=makeQuery(id+"F6.boolean.opBoolean","COPY",EDGE,{"derivedFrom":makeQuery(id+"F6.opExtrude","SWEPT_EDGE",EDGE,{"disambiguationData":[OSD([sQuery(id+"F5.wireOp",EDGE,"E24.left"),sQuery(id+"F5.wireOp",EDGE,"E30.top"),sQuery(id+"F5.wireOp",EDGE,"E30.left")])]})});
            var Q32;
            Q32=makeQuery(id+"F6.boolean.opBoolean","COPY",EDGE,{"derivedFrom":makeQuery(id+"F6.opExtrude","SWEPT_EDGE",EDGE,{"disambiguationData":[OSD([sQuery(id+"F5.wireOp",EDGE,"E24.left"),sQuery(id+"F5.wireOp",EDGE,"E30.bottom"),sQuery(id+"F5.wireOp",EDGE,"E30.left")])]})});
            var Q33;
            Q33=makeQuery(id+"F6.boolean.opBoolean","COPY",EDGE,{"derivedFrom":makeQuery(id+"F6.opExtrude","SWEPT_EDGE",EDGE,{"disambiguationData":[OSD([sQuery(id+"F5.wireOp",EDGE,"E24.top"),sQuery(id+"F5.wireOp",EDGE,"E24.right")])]})});
            var Q34;
            Q34=makeQuery(id+"F6.boolean.opBoolean","COPY",EDGE,{"derivedFrom":makeQuery(id+"F6.opExtrude","SWEPT_EDGE",EDGE,{"disambiguationData":[OSD([sQuery(id+"F5.wireOp",EDGE,"E24.bottom"),sQuery(id+"F5.wireOp",EDGE,"E24.right")])]})});
            var Q35;
            Q35=makeQuery(id+"F6.boolean.opBoolean","COPY",EDGE,{"derivedFrom":makeQuery(id+"F6.opExtrude","SWEPT_EDGE",EDGE,{"disambiguationData":[OSD([sQuery(id+"F5.wireOp",EDGE,"E24.bottom"),sQuery(id+"F5.wireOp",EDGE,"E24.left")])]})});
            var Q36;
            Q36=makeQuery(id+"F6.boolean.opBoolean","COPY",EDGE,{"derivedFrom":makeQuery(id+"F6.opExtrude","SWEPT_EDGE",EDGE,{"disambiguationData":[OSD([sQuery(id+"F5.wireOp",EDGE,"E24.top"),sQuery(id+"F5.wireOp",EDGE,"E24.left")])]})});
            var Q37;
            Q37=makeQuery(id+"F6.boolean.opBoolean","COPY",EDGE,{"derivedFrom":makeQuery(id+"F6.opExtrude","SWEPT_EDGE",EDGE,{"disambiguationData":[OSD([sQuery(id+"F5.wireOp",EDGE,"E27.MirrorCS"),sQuery(id+"F5.wireOp",EDGE,"E28.MirrorCS")])]})});
            var Q38;
            Q38=makeQuery(id+"F6.boolean.opBoolean","COPY",EDGE,{"derivedFrom":makeQuery(id+"F6.opExtrude","SWEPT_EDGE",EDGE,{"disambiguationData":[OSD([sQuery(id+"F5.wireOp",EDGE,"E26.MirrorCS"),sQuery(id+"F5.wireOp",EDGE,"E27.MirrorCS")])]})});
            var Q39;
            {var subQ0=sQuery(id+"F0.wireOp",EDGE,"E9.MirrorCS");var subQ1=sQuery(id+"F0.wireOp",EDGE,"E8.MirrorCS");var subQ2=sQuery(id+"F0.wireOp",EDGE,"E7.MirrorCS");var subQ3=sQuery(id+"F0.wireOp",EDGE,"E6.MirrorCS");var subQ4=sQuery(id+"F0.wireOp",EDGE,"E2");var subQ5=sQuery(id+"F0.wireOp",EDGE,"E4.MirrorCS");var subQ6=sQuery(id+"F0.wireOp",EDGE,"E3");var subQ7=sQuery(id+"F0.wireOp",EDGE,"E5.MirrorCS");Q39=makeQuery(id+"F6.boolean.opBoolean","INTERSECT",EDGE,{"derivedFrom":[makeQuery(id+"F3.opBoolean","SPLIT",FACE,{"disambiguationData":[TD([makeQuery(id+"F1.opExtrude","SWEPT_FACE",FACE,{"disambiguationData":[OSD([subQ4])]})])],"derivedFrom":makeQuery(id+"F2.opExtrude","CAP_FACE",FACE,{"disambiguationData":[OSD([subQ4,subQ6,subQ5,subQ7,subQ3,subQ2,subQ1,subQ0])],"isStart":true})}),makeQuery(id+"F6.opExtrude","SWEPT_FACE",FACE,{"disambiguationData":[OSD([sQuery(id+"F5.wireOp",EDGE,"E27.MirrorCS")])]})]});}
            var Q40;
            Q40=makeQuery(id+"F6.boolean.opBoolean","COPY",EDGE,{"derivedFrom":makeQuery(id+"F6.opExtrude","SWEPT_EDGE",EDGE,{"disambiguationData":[OSD([sQuery(id+"F5.wireOp",EDGE,"E32.MirrorCS"),sQuery(id+"F5.wireOp",EDGE,"E33.MirrorCS")])]})});
            var Q41;
            {var subQ0=sQuery(id+"F0.wireOp",EDGE,"E9.MirrorCS");var subQ1=sQuery(id+"F0.wireOp",EDGE,"E8.MirrorCS");var subQ2=sQuery(id+"F0.wireOp",EDGE,"E7.MirrorCS");var subQ3=sQuery(id+"F0.wireOp",EDGE,"E6.MirrorCS");var subQ4=sQuery(id+"F0.wireOp",EDGE,"E2");var subQ5=sQuery(id+"F0.wireOp",EDGE,"E4.MirrorCS");var subQ6=sQuery(id+"F0.wireOp",EDGE,"E3");var subQ7=sQuery(id+"F0.wireOp",EDGE,"E5.MirrorCS");Q41=makeQuery(id+"F6.boolean.opBoolean","INTERSECT",EDGE,{"derivedFrom":[makeQuery(id+"F3.opBoolean","SPLIT",FACE,{"disambiguationData":[TD([makeQuery(id+"F1.opExtrude","SWEPT_FACE",FACE,{"disambiguationData":[OSD([subQ4])]})])],"derivedFrom":makeQuery(id+"F2.opExtrude","CAP_FACE",FACE,{"disambiguationData":[OSD([subQ4,subQ6,subQ5,subQ7,subQ3,subQ2,subQ1,subQ0])],"isStart":true})}),makeQuery(id+"F6.opExtrude","SWEPT_FACE",FACE,{"disambiguationData":[OSD([sQuery(id+"F5.wireOp",EDGE,"E32.MirrorCS")])]})]});}
            var Q42;
            {var subQ0=sQuery(id+"F0.wireOp",EDGE,"E9.MirrorCS");var subQ1=sQuery(id+"F0.wireOp",EDGE,"E8.MirrorCS");var subQ2=sQuery(id+"F0.wireOp",EDGE,"E7.MirrorCS");var subQ3=sQuery(id+"F0.wireOp",EDGE,"E6.MirrorCS");var subQ4=sQuery(id+"F0.wireOp",EDGE,"E2");var subQ5=sQuery(id+"F0.wireOp",EDGE,"E4.MirrorCS");var subQ6=sQuery(id+"F0.wireOp",EDGE,"E3");var subQ7=sQuery(id+"F0.wireOp",EDGE,"E5.MirrorCS");Q42=makeQuery(id+"F6.boolean.opBoolean","INTERSECT",EDGE,{"derivedFrom":[makeQuery(id+"F3.opBoolean","SPLIT",FACE,{"disambiguationData":[TD([makeQuery(id+"F1.opExtrude","SWEPT_FACE",FACE,{"disambiguationData":[OSD([subQ4])]})])],"derivedFrom":makeQuery(id+"F2.opExtrude","CAP_FACE",FACE,{"disambiguationData":[OSD([subQ4,subQ6,subQ5,subQ7,subQ3,subQ2,subQ1,subQ0])],"isStart":true})}),makeQuery(id+"F6.opExtrude","SWEPT_FACE",FACE,{"disambiguationData":[OSD([sQuery(id+"F5.wireOp",EDGE,"E33.MirrorCS")])]})]});}
            var Q43;
            {var subQ0=sQuery(id+"F0.wireOp",EDGE,"E9.MirrorCS");var subQ1=sQuery(id+"F0.wireOp",EDGE,"E8.MirrorCS");var subQ2=sQuery(id+"F0.wireOp",EDGE,"E7.MirrorCS");var subQ3=sQuery(id+"F0.wireOp",EDGE,"E6.MirrorCS");var subQ4=sQuery(id+"F0.wireOp",EDGE,"E2");var subQ5=sQuery(id+"F0.wireOp",EDGE,"E4.MirrorCS");var subQ6=sQuery(id+"F0.wireOp",EDGE,"E3");var subQ7=sQuery(id+"F0.wireOp",EDGE,"E5.MirrorCS");Q43=makeQuery(id+"F6.boolean.opBoolean","INTERSECT",EDGE,{"derivedFrom":[makeQuery(id+"F3.opBoolean","SPLIT",FACE,{"disambiguationData":[TD([makeQuery(id+"F1.opExtrude","SWEPT_FACE",FACE,{"disambiguationData":[OSD([subQ4])]})])],"derivedFrom":makeQuery(id+"F2.opExtrude","CAP_FACE",FACE,{"disambiguationData":[OSD([subQ4,subQ6,subQ5,subQ7,subQ3,subQ2,subQ1,subQ0])],"isStart":true})}),makeQuery(id+"F6.opExtrude","SWEPT_FACE",FACE,{"disambiguationData":[OSD([sQuery(id+"F5.wireOp",EDGE,"E34.MirrorCS")])]})]});}
            var Q44;
            Q44=makeQuery(id+"F6.boolean.opBoolean","COPY",EDGE,{"derivedFrom":makeQuery(id+"F6.opExtrude","SWEPT_EDGE",EDGE,{"disambiguationData":[OSD([sQuery(id+"F5.wireOp",EDGE,"E28.MirrorCS"),sQuery(id+"F5.wireOp",EDGE,"E34.MirrorCS")])]})});
            var Q45;
            {var subQ0=sQuery(id+"F5.wireOp",EDGE,"E28.MirrorCS");var subQ1=sQuery(id+"F0.wireOp",EDGE,"E9.MirrorCS");var subQ2=sQuery(id+"F0.wireOp",EDGE,"E8.MirrorCS");var subQ3=sQuery(id+"F0.wireOp",EDGE,"E7.MirrorCS");var subQ4=sQuery(id+"F0.wireOp",EDGE,"E6.MirrorCS");var subQ5=sQuery(id+"F0.wireOp",EDGE,"E2");var subQ6=sQuery(id+"F0.wireOp",EDGE,"E4.MirrorCS");var subQ7=sQuery(id+"F0.wireOp",EDGE,"E3");var subQ8=sQuery(id+"F0.wireOp",EDGE,"E5.MirrorCS");Q45=makeQuery(id+"F6.boolean.opBoolean","INTERSECT",EDGE,{"derivedFrom":[makeQuery(id+"F3.opBoolean","SPLIT",FACE,{"disambiguationData":[TD([makeQuery(id+"F1.opExtrude","SWEPT_FACE",FACE,{"disambiguationData":[OSD([subQ5])]})])],"derivedFrom":makeQuery(id+"F2.opExtrude","CAP_FACE",FACE,{"disambiguationData":[OSD([subQ5,subQ7,subQ6,subQ8,subQ4,subQ3,subQ2,subQ1])],"isStart":true})}),makeQuery(id+"F6.opExtrude","SWEPT_FACE",FACE,{"disambiguationData":[OSD([subQ0]),TDD([makeQuery(id+"F5.imprint","IMPRINT",EDGE,{"disambiguationData":[TD([[makeQuery(id+"F5.imprint","INTERSECT",VERTEX,{"derivedFrom":[subQ0,sQuery(id+"F5.wireOp",EDGE,"E29.MirrorCS")]}),-1.0]])],"derivedFrom":subQ0})])]})]});}
            var Q46;
            {var subQ0=sQuery(id+"F0.wireOp",EDGE,"E9.MirrorCS");var subQ1=sQuery(id+"F0.wireOp",EDGE,"E8.MirrorCS");var subQ2=sQuery(id+"F0.wireOp",EDGE,"E7.MirrorCS");var subQ3=sQuery(id+"F0.wireOp",EDGE,"E6.MirrorCS");var subQ4=sQuery(id+"F0.wireOp",EDGE,"E2");var subQ5=sQuery(id+"F0.wireOp",EDGE,"E4.MirrorCS");var subQ6=sQuery(id+"F0.wireOp",EDGE,"E3");var subQ7=sQuery(id+"F0.wireOp",EDGE,"E5.MirrorCS");Q46=makeQuery(id+"F6.boolean.opBoolean","INTERSECT",EDGE,{"derivedFrom":[makeQuery(id+"F3.opBoolean","SPLIT",FACE,{"disambiguationData":[TD([makeQuery(id+"F1.opExtrude","SWEPT_FACE",FACE,{"disambiguationData":[OSD([subQ4])]})])],"derivedFrom":makeQuery(id+"F2.opExtrude","CAP_FACE",FACE,{"disambiguationData":[OSD([subQ4,subQ6,subQ5,subQ7,subQ3,subQ2,subQ1,subQ0])],"isStart":true})}),makeQuery(id+"F6.opExtrude","SWEPT_FACE",FACE,{"disambiguationData":[OSD([sQuery(id+"F5.wireOp",EDGE,"E29.MirrorCS")])]})]});}
            var Q47;
            {var subQ0=sQuery(id+"F0.wireOp",EDGE,"E9.MirrorCS");var subQ1=sQuery(id+"F0.wireOp",EDGE,"E8.MirrorCS");var subQ2=sQuery(id+"F0.wireOp",EDGE,"E7.MirrorCS");var subQ3=sQuery(id+"F0.wireOp",EDGE,"E6.MirrorCS");var subQ4=sQuery(id+"F0.wireOp",EDGE,"E2");var subQ5=sQuery(id+"F0.wireOp",EDGE,"E4.MirrorCS");var subQ6=sQuery(id+"F0.wireOp",EDGE,"E3");var subQ7=sQuery(id+"F0.wireOp",EDGE,"E5.MirrorCS");Q47=makeQuery(id+"F6.boolean.opBoolean","INTERSECT",EDGE,{"derivedFrom":[makeQuery(id+"F3.opBoolean","SPLIT",FACE,{"disambiguationData":[TD([makeQuery(id+"F1.opExtrude","SWEPT_FACE",FACE,{"disambiguationData":[OSD([subQ4])]})])],"derivedFrom":makeQuery(id+"F2.opExtrude","CAP_FACE",FACE,{"disambiguationData":[OSD([subQ4,subQ6,subQ5,subQ7,subQ3,subQ2,subQ1,subQ0])],"isStart":true})}),makeQuery(id+"F6.opExtrude","SWEPT_FACE",FACE,{"disambiguationData":[OSD([sQuery(id+"F5.wireOp",EDGE,"E26.MirrorCS")])]})]});}
            var Q48;
            Q48=makeQuery(id+"F6.boolean.opBoolean","COPY",EDGE,{"derivedFrom":makeQuery(id+"F6.opExtrude","SWEPT_EDGE",EDGE,{"disambiguationData":[OSD([sQuery(id+"F5.wireOp",EDGE,"E26.MirrorCS"),sQuery(id+"F5.wireOp",EDGE,"E29.MirrorCS")])]})});
            var Q49;
            Q49=makeQuery(id+"F6.boolean.opBoolean","COPY",EDGE,{"derivedFrom":makeQuery(id+"F6.opExtrude","SWEPT_EDGE",EDGE,{"disambiguationData":[OSD([sQuery(id+"F5.wireOp",EDGE,"E28.MirrorCS"),sQuery(id+"F5.wireOp",EDGE,"E29.MirrorCS")])]})});
            var Q50;
            Q50=makeQuery(id+"F6.boolean.opBoolean","COPY",EDGE,{"derivedFrom":makeQuery(id+"F6.opExtrude","SWEPT_EDGE",EDGE,{"disambiguationData":[OSD([sQuery(id+"F5.wireOp",EDGE,"E33.MirrorCS"),sQuery(id+"F5.wireOp",EDGE,"E34.MirrorCS")])]})});
            var Q51;
            Q51=makeQuery(id+"F1.opExtrude","SWEPT_EDGE",EDGE,{"disambiguationData":[OSD([sQuery(id+"F0.wireOp",EDGE,"E16.MirrorCS"),sQuery(id+"F0.wireOp",EDGE,"E17.MirrorCS")])]});
            var Q52;
            Q52=makeQuery(id+"F2.opExtrude","CAP_EDGE",EDGE,{"disambiguationData":[OSD([sQuery(id+"F0.wireOp",EDGE,"E2"),sQuery(id+"F0.wireOp",EDGE,"E8.MirrorCS")])],"isStart":true});
            var Q53;
            Q53=makeQuery(id+"F2.opExtrude","CAP_EDGE",EDGE,{"disambiguationData":[OSD([sQuery(id+"F0.wireOp",EDGE,"E7.MirrorCS"),sQuery(id+"F0.wireOp",EDGE,"E9.MirrorCS")])],"isStart":true});
            var Q54;
            Q54=makeQuery(id+"F4.opFillet","BLEND_EDGE",EDGE,{"blendedFrom":[makeQuery(id+"F1.opExtrude","CAP_EDGE",EDGE,{"disambiguationData":[OSD([sQuery(id+"F0.wireOp",EDGE,"E14.MirrorCS")])],"isStart":false}),makeQuery(id+"F1.opExtrude","SWEPT_FACE",FACE,{"disambiguationData":[OSD([sQuery(id+"F0.wireOp",EDGE,"E15.MirrorCS")])]})],"blendedInto":[makeQuery(id+"F1.opExtrude","SWEPT_FACE",FACE,{"disambiguationData":[OSD([sQuery(id+"F0.wireOp",EDGE,"E15.MirrorCS")])]})]});
            var Q55;
            Q55=makeQuery(id+"F4.opFillet","BLEND_EDGE",EDGE,{"blendedFrom":[makeQuery(id+"F1.opExtrude","CAP_EDGE",EDGE,{"disambiguationData":[OSD([sQuery(id+"F0.wireOp",EDGE,"E13.MirrorCS")])],"isStart":false}),makeQuery(id+"F1.opExtrude","SWEPT_FACE",FACE,{"disambiguationData":[OSD([sQuery(id+"F0.wireOp",EDGE,"E12.MirrorCS")])]})],"blendedInto":[makeQuery(id+"F1.opExtrude","SWEPT_FACE",FACE,{"disambiguationData":[OSD([sQuery(id+"F0.wireOp",EDGE,"E12.MirrorCS")])]})]});
            var Q56;
            Q56=makeQuery(id+"F1.opExtrude","SWEPT_EDGE",EDGE,{"disambiguationData":[OSD([sQuery(id+"F0.wireOp",EDGE,"E10"),sQuery(id+"F0.wireOp",EDGE,"E11")])]});
            fillet(context, id + "F7", {"entities" : qUnion([Q0, Q1, Q2, Q3, Q4, Q5, Q6, Q7, Q8, Q9, Q10, Q11, Q12, Q13, Q14, Q15, Q16, Q17, Q18, Q19, Q20, Q21, Q22, Q23, Q24, Q25, Q26, Q27, Q28, Q29, Q30, Q31, Q32, Q33, Q34, Q35, Q36, Q37, Q38, Q39, Q40, Q41, Q42, Q43, Q44, Q45, Q46, Q47, Q48, Q49, Q50, Q51, Q52, Q53, Q54, Q55, Q56]), "radius" : 1 * mm, "tangentPropagation" : true, "allowEdgeOverflow" : false});
        }
    });
